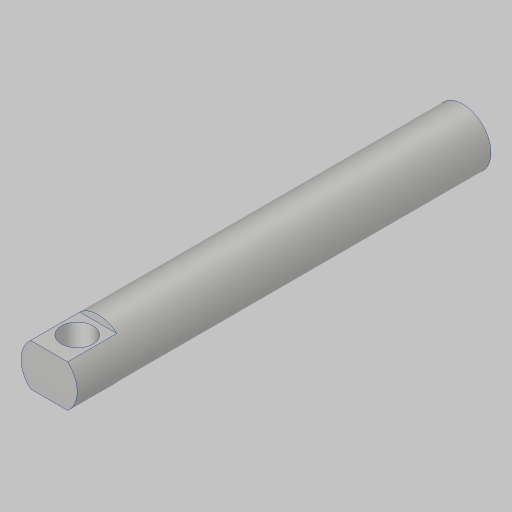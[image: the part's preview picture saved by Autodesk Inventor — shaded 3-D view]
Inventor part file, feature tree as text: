
AUTODESK INVENTOR PART (.ipt)
format: ipt  version: 2023.5 (Build 275446000, 446)  size: 112,128 bytes
history: native  units: in
note: dims shown in document units (in); Inventor stores cm internally (conversion verified against a paired STEP export)
features: sketch x3, extrude x2, hole x1, projected_geometry x1
ambient origin geometry x8: Origin, YZ Plane, XZ Plane, XY Plane, X Axis, Y Axis, Z Axis, Center Point
bodies: Solid1 (feature_tree)
feature tree (7):
  extrude  "Extrusion1"  Depth=2.323in TaperAngle=0.0deg
  extrude  "Extrusion2"  Depth=0.276in TaperAngle=0.0deg
  hole  "Hole1"  [1 undecoded]
  sketch  "Sketch1"  dims[d0=0.315in d1=2.323in d2=0.0in]
  sketch  "Sketch2"  dims[d3=0.2362in d4=0.276in d5=0.0in]
  projected_geometry  "Projected Loop1"
  sketch  "Sketch3"  dims[d6=0.1181in d7=0.177in d8=0.328in d9=0.332in d10=0.25in d11=0.5635in d12=1.0in d13=0.8108in]
note: 1 required parameter value undecoded (feature->parameter linkage not recoverable at this tier; creation-order binding heuristic only, values carry confidence <= 0.55)
